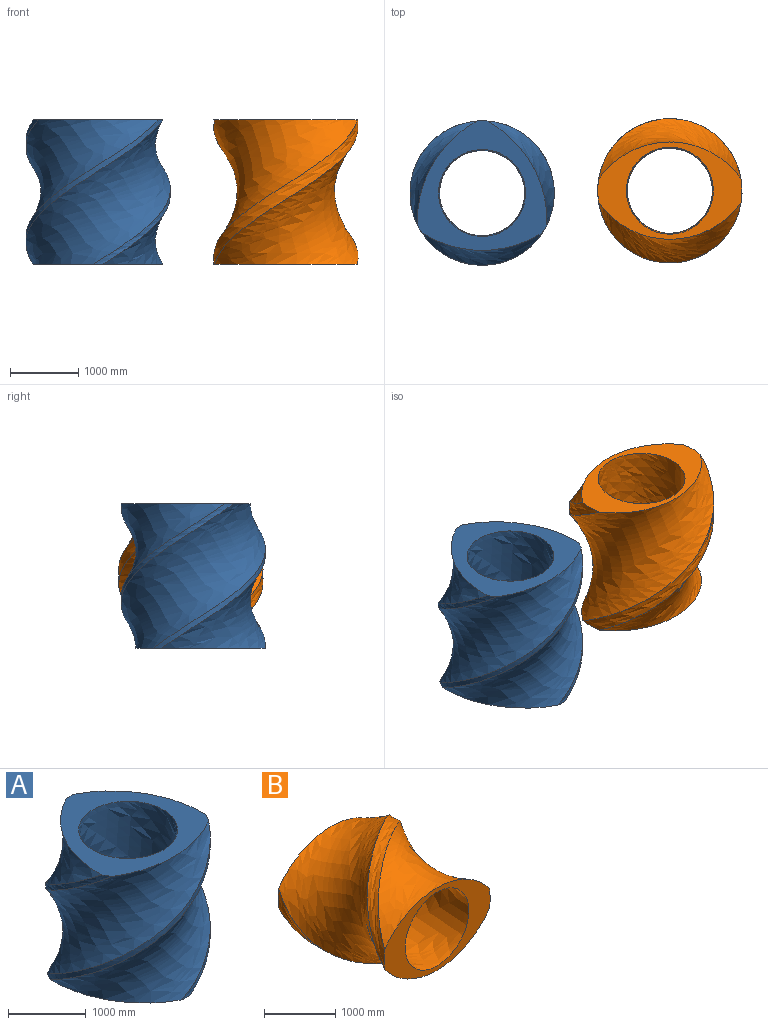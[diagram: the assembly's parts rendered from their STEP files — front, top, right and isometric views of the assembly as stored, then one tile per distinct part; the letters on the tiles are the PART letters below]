
ASSEMBLY  parts=2 mates=1
PART A: 9 faces, bbox 2844.6x2840.1x2186.3 mm
  f0: bspline ~2186.28x2111.69mm, area 4155573.8mm2, adj f1,f5,f6,f7
  f1: bspline ~2186.28x2050.3mm, area 297262.7mm2, adj f0,f2,f6,f7
  f2: bspline ~2186.28x2111.69mm, area 4155573.8mm2, adj f1,f3,f6,f7
  f3: bspline ~2186.28x2112.51mm, area 297262.7mm2, adj f2,f4,f6,f7
  f4: bspline ~2186.28x2109.19mm, area 4155573.8mm2, adj f3,f5,f6,f7
  f5: bspline ~2186.28x2002.73mm, area 297262.7mm2, adj f0,f4,f6,f7
  f6: plane 1894.19x1892.3mm, normal (0,0,-1), area 1392382.1mm2, adj f0,f1,f2,f3,f4,f5,f8
  f7: plane 1894.19x1892.3mm, normal (0,0,1), area 1392382.1mm2, adj f0,f1,f2,f3,f4,f5,f8
  f8: bspline ~2844.61x2840.1mm, area 8409491mm2, adj f6,f7
PART B: 7 faces, bbox 2840.1x2186.3x2844.6 mm
  f0: bspline ~2186.28x2124.08mm, area 718152.3mm2, adj f1,f3,f4,f5
  f1: bspline ~2186.28x2156.98mm, area 5566883.8mm2, adj f0,f2,f4,f5
  f2: bspline ~2186.28x2124.08mm, area 718152.3mm2, adj f1,f3,f4,f5
  f3: bspline ~2186.28x2156.98mm, area 5566883.8mm2, adj f0,f2,f4,f5
  f4: plane 2108.2x1422.4mm, normal (0,1,0), area 1026325.9mm2, adj f0,f1,f2,f3,f6
  f5: plane 2108.2x1422.4mm, normal (0,-1,0), area 1026325.9mm2, adj f0,f1,f2,f3,f6
  f6: bspline ~2844.61x2840.1mm, area 8409491mm2, adj f4,f5
PLACE A t=(-1701.8,-203.2,-2108.2)mm
PLACE B rot(axis=(-1,0,0),90deg) t=(1040.37,-169.57,-2108.2)mm
MATE planar A.f7 <-> B.f5  axis (0,0,1) through (-1701.8,-203.2,0)mm
